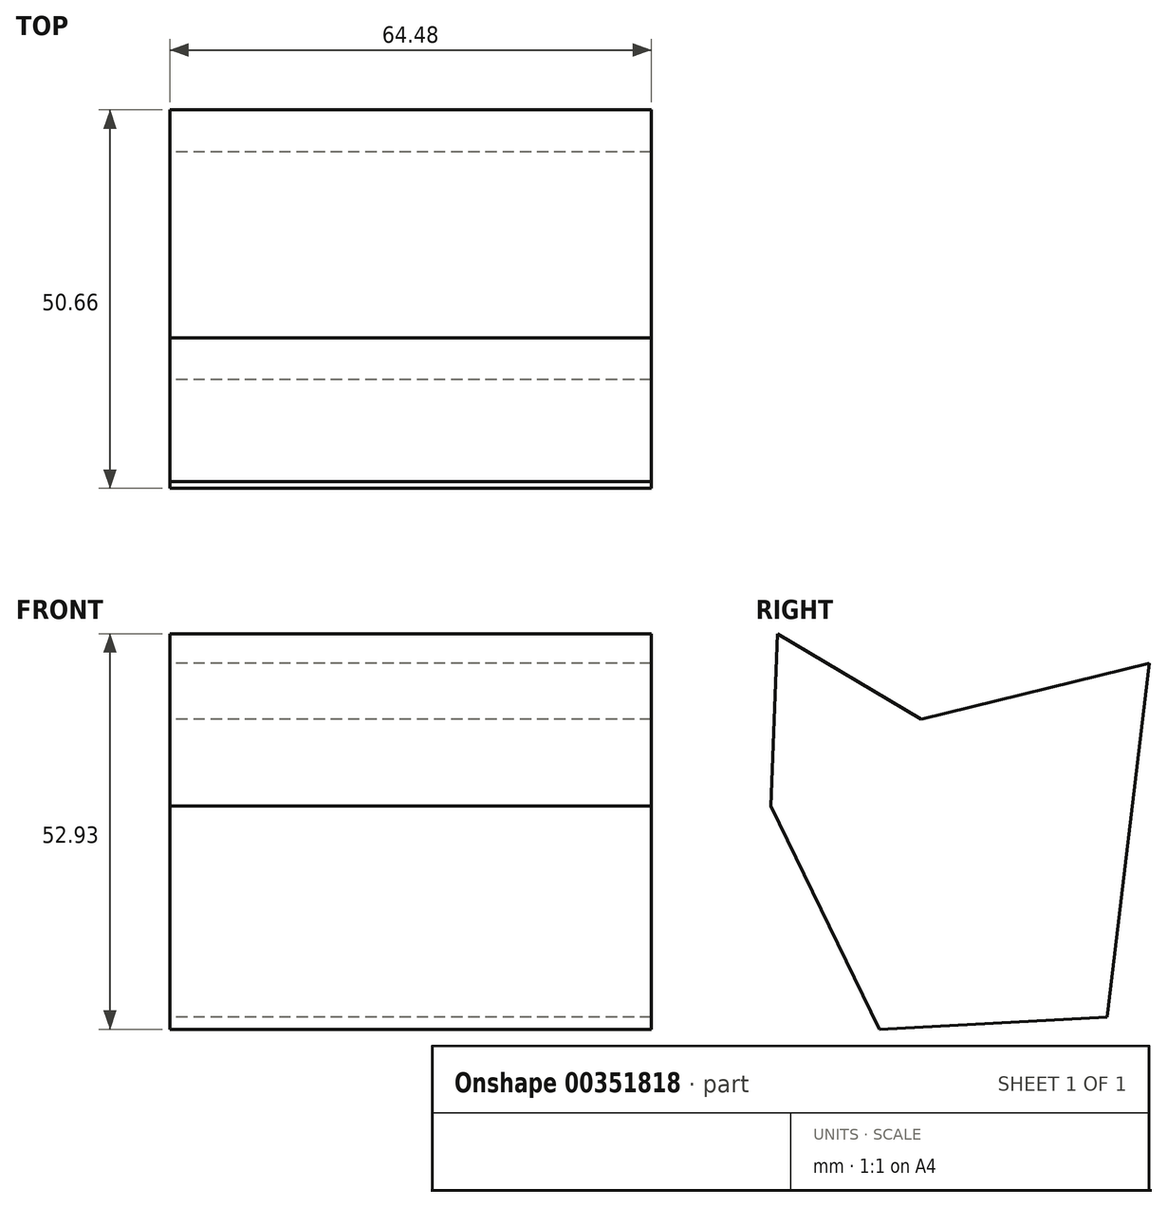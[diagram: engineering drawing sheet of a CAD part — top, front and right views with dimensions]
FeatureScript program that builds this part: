
annotation { "Feature Type Name" : "Feature", "Feature Type Description" : "" }
export const myFeature = defineFeature(function(context is Context, id is Id, definition is map)
    precondition{}
    {
        {
            var Q0;
            Q0=qCreatedBy(makeId("Right.planeOp"),FACE);
            var sketch = newSketch(context, id + "F0", { "sketchPlane" : qUnion([Q0])});
            skLineSegment(sketch, "E0", {"start": v(-19.78, 63.34) * mm, "end": v(0, 51.62) * mm});
            skLineSegment(sketch, "E1", {"start": v(0, 51.62) * mm, "end": v(30.56, 59.07) * mm});
            skLineSegment(sketch, "E2", {"start": v(30.56, 59.07) * mm, "end": v(24.94, 11.7) * mm});
            skLineSegment(sketch, "E3", {"start": v(24.94, 11.7) * mm, "end": v(-5.54, 10.09) * mm});
            skLineSegment(sketch, "E4", {"start": v(-5.54, 10.09) * mm, "end": v(-20.1, 39.97) * mm});
            skLineSegment(sketch, "E5", {"start": v(-20.1, 39.97) * mm, "end": v(-19.18, 64.71) * mm});
            skLineSegment(sketch, "E6", {"start": v(-19.18, 64.71) * mm, "end": v(-19.78, 63.34) * mm});
            skSolve(sketch);
        }
        {
            var Q0;
            {var subQ0=sQuery(id+"F0.wireOp",EDGE,"E1");Q0=makeQuery(id+"F0.imprint","IMPRINT",FACE,{"disambiguationData":[TD([[makeQuery(id+"F0.imprint","IMPRINT",EDGE,{"derivedFrom":subQ0}),-1.0]])]});}
            var sketch = newSketch(context, id + "F1", { "sketchPlane" : qUnion([Q0])});
            skSolve(sketch);
        }
        {
            var Q0;
            {var subQ0=sQuery(id+"F0.wireOp",EDGE,"E1");Q0=makeQuery(id+"F1.imprint","IMPRINT",FACE,{"disambiguationData":[TD([[makeQuery(id+"F1.imprint","IMPRINT",EDGE,{"derivedFrom":makeQuery(id+"F0.imprint","IMPRINT",EDGE,{"derivedFrom":subQ0})}),-1.0]])]});}
            extrude(context, id + "F2", {"entities" : qUnion([Q0]), "depth" : 64.48 * mm, "offsetDistance" : 25.4 * mm});
        }
    });
